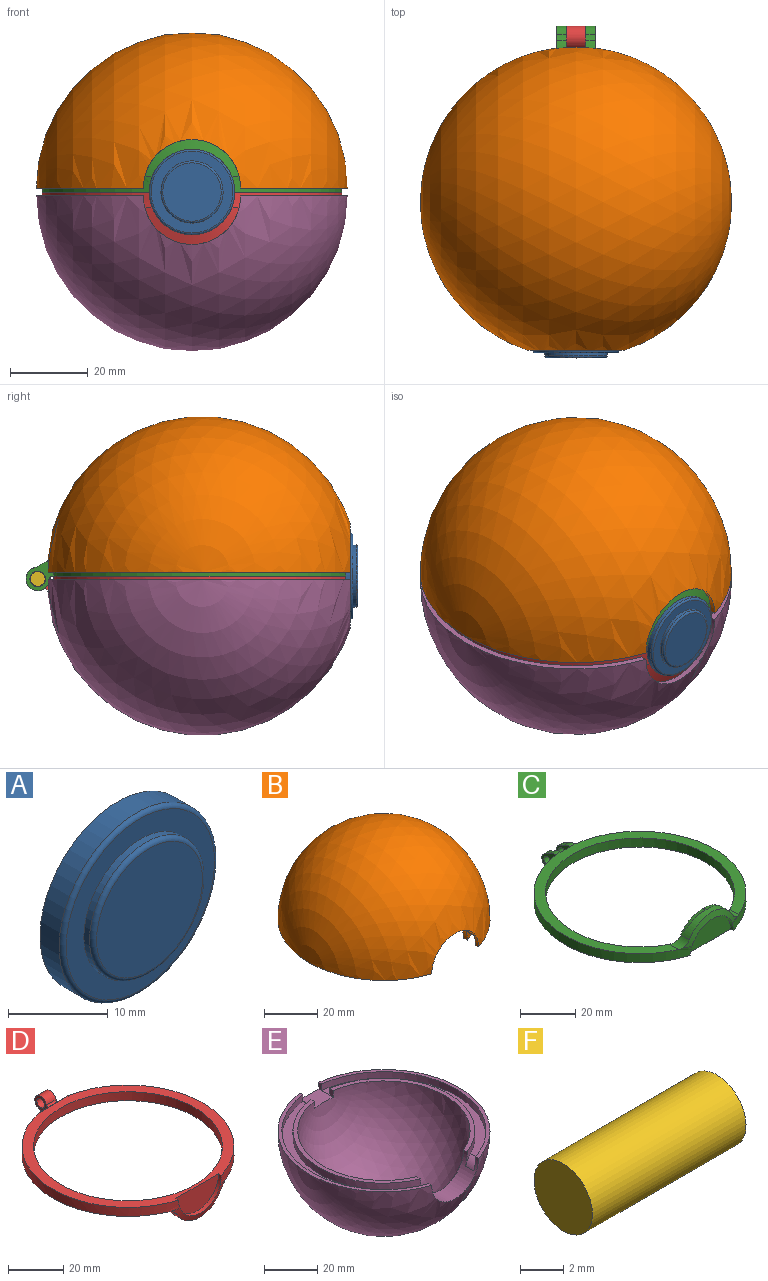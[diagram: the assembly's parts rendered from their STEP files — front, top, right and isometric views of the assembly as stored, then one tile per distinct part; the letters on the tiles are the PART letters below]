
ASSEMBLY  parts=6 mates=5
PART A: 7 faces, bbox 23.8x4.5x23.8 mm
  f0: cylinder r=11mm len=22mm, axis (0,1,0), area 186.6mm2, adj f2,f6
  f1: plane 21x21mm, normal (0,-1,0), area 145.3mm2, adj f3,f6
  f2: plane 22x22mm, normal (0,1,0), area 380.1mm2, adj f0
  f3: cylinder r=8mm len=16mm, axis (0,1,0), area 40.2mm2, adj f1,f5
  f4: plane 15x15mm, normal (0,-1,0), area 176.7mm2, adj f5
  f5: torus R=7.5mm, axis (0,-1,0), area 38.6mm2, adj f3,f4
  f6: torus R=10.5mm, axis (0,-1,0), area 53.4mm2, adj f0,f1
PART B: 18 faces, bbox 80x80x40 mm
  f0: plane 65.88x29.3mm, normal (0,0,-1), area 156.8mm2, adj f1,f8,f12,f17
  f1: sphere r=32.5mm, area 6350.2mm2, adj f0,f7,f12,f15,f16,f17
  f2: cylinder r=34.3mm len=66.38mm, axis (0,0,-1), area 272.3mm2, adj f4,f7,f12,f14,f16
  f3: cylinder r=38.5mm len=75.03mm, axis (0,0,-1), area 312mm2, adj f4,f11,f12,f14,f16
  f4: plane 73.39x33.5mm, normal (0,0,-1), area 391.7mm2, adj f2,f3,f14,f16
  f5: sphere r=40mm, area 9770.1mm2, adj f6,f11,f12,f15,f16,f17
  f6: plane 77.68x35mm, normal (0,0,-1), area 158.4mm2, adj f5,f9,f12,f17
  f7: plane 65.88x29.3mm, normal (0,0,-1), area 156.8mm2, adj f1,f2,f12,f16
  f8: cylinder r=34.3mm len=66.38mm, axis (0,0,-1), area 272.3mm2, adj f0,f10,f12,f13,f17
  f9: cylinder r=38.5mm len=75.03mm, axis (0,0,-1), area 312mm2, adj f6,f10,f12,f13,f17
  f10: plane 73.39x33.5mm, normal (0,0,-1), area 391.7mm2, adj f8,f9,f13,f17
  f11: plane 77.68x35mm, normal (0,0,-1), area 158.4mm2, adj f3,f5,f12,f16
  f12: cylinder r=12.5mm len=25mm, axis (0,1,0), area 261.2mm2, adj f0,f1,f2,f3,f5,f6,f7,f8
  f13: cylinder r=5mm len=6.29mm, axis (0,1,0), area 24.7mm2, adj f8,f9,f10,f12
  f14: cylinder r=5mm len=6.29mm, axis (0,1,0), area 24.7mm2, adj f2,f3,f4,f12
  f15: plane 10.05x7.97mm, normal (0,0,-1), area 75.5mm2, adj f1,f5,f16,f17
  f16: plane 7.72x3.1mm, normal (-1,0,0), area 10.8mm2, adj f1,f2,f3,f4,f5,f7,f11,f15
  f17: plane 7.72x3.1mm, normal (1,0,0), area 10.8mm2, adj f0,f1,f5,f6,f8,f9,f10,f15
PART C: 30 faces, bbox 77x85.6x18.1 mm
  f0: cylinder r=5mm len=2.5mm, axis (1,0,0), area 4.7mm2, adj f2,f20,f22,f28
  f1: cylinder r=1mm len=2.5mm, axis (-1,0,0), area 3.8mm2, adj f3,f5,f21,f27
  f2: cylinder r=5mm len=3.04mm, axis (1,0,0), area 8.2mm2, adj f0,f10,f20,f28
  f3: cylinder r=3mm len=5.99mm, axis (-1,0,0), area 32.8mm2, adj f1,f21,f24,f27
  f4: cylinder r=2mm len=4mm, axis (-1,0,0), area 31.4mm2, adj f21,f27
  f5: plane 77x75.26mm, normal (0,0,-1), area 905mm2, adj f1,f6,f8,f9,f18,f19,f20,f21
  f6: cylinder r=38.5mm len=75.29mm, axis (0,0,-1), area 421.3mm2, adj f5,f10,f12,f16,f19,f21
  f7: plane 1.93x0.79mm, normal (0,0.26,0.96), area 1.3mm2, adj f11,f13,f14,f15
  f8: cylinder r=34.3mm len=68.6mm, axis (0,0,-1), area 863.2mm2, adj f5,f10,f11,f16,f17
  f9: cylinder r=38.5mm len=75.29mm, axis (0,0,-1), area 421.3mm2, adj f5,f10,f12,f17,f19,f20
  f10: plane 77x73.68mm, normal (0,0,1), area 824.7mm2, adj f2,f6,f8,f9,f16,f17,f20,f21
  f11: bspline ~27.63x8.98mm, area 174.8mm2, adj f7,f8,f13,f14,f15,f16,f17
  f12: bspline ~27.97x10.28mm, area 75.1mm2, adj f6,f9,f15,f16,f17,f19
  f13: bspline ~14.62x12.35mm, area 19.7mm2, adj f7,f11,f15
  f14: bspline ~14.67x12.38mm, area 19.6mm2, adj f7,f11,f15
  f15: cylinder r=12.5mm len=22.24mm, axis (0,1,0), area 84.3mm2, adj f7,f11,f12,f13,f14,f16,f17
  f16: cylinder r=5mm len=5.97mm, axis (0,1,0), area 24.8mm2, adj f6,f8,f10,f11,f12,f15
  f17: cylinder r=5mm len=5.97mm, axis (0,1,0), area 24.8mm2, adj f8,f9,f10,f11,f12,f15
  f18: plane 22x11mm, normal (0,-1,0), area 190.1mm2, adj f5,f19
  f19: cylinder r=11mm len=22mm, axis (0,-1,0), area 54.8mm2, adj f5,f6,f9,f12,f18
  f20: plane 7.75x7.18mm, normal (1,0,0), area 25.8mm2, adj f0,f2,f5,f9,f10,f22,f23,f25
  f21: plane 7.75x7.18mm, normal (-1,0,0), area 25.8mm2, adj f1,f3,f4,f5,f6,f10,f24,f26
  f22: cylinder r=3mm len=5.99mm, axis (-1,0,0), area 32.8mm2, adj f0,f20,f25,f28
  f23: cylinder r=2mm len=4mm, axis (-1,0,0), area 31.4mm2, adj f20,f28
  f24: cylinder r=5mm len=2.5mm, axis (1,0,0), area 4.7mm2, adj f3,f21,f26,f27
  f25: cylinder r=1mm len=2.5mm, axis (-1,0,0), area 3.8mm2, adj f5,f20,f22,f28
  f26: cylinder r=5mm len=3.04mm, axis (1,0,0), area 8.2mm2, adj f10,f21,f24,f27
  f27: plane 7.75x7.18mm, normal (1,0,0), area 25.8mm2, adj f1,f3,f4,f5,f10,f24,f26,f29
  f28: plane 7.75x7.18mm, normal (-1,0,0), area 25.8mm2, adj f0,f2,f5,f10,f22,f23,f25,f29
  f29: plane 5x4mm, normal (0,1,0), area 20mm2, adj f5,f10,f27,f28
PART D: 25 faces, bbox 77x85.9x16.7 mm
  f0: cylinder r=2mm len=5mm, axis (-1,0,0), area 62.8mm2, adj f22,f24
  f1: cylinder r=3mm len=6mm, axis (-1,0,0), area 77.9mm2, adj f3,f20,f22,f24
  f2: cylinder r=0.5mm len=5mm, axis (1,0,0), area 3.9mm2, adj f3,f19,f22,f24
  f3: cylinder r=1mm len=5mm, axis (1,0,0), area 5.7mm2, adj f1,f2,f22,f24
  f4: plane 77x74.57mm, normal (0,0,1), area 897.5mm2, adj f5,f8,f9,f15,f16,f19
  f5: cylinder r=38.5mm len=75.29mm, axis (0,0,1), area 420.5mm2, adj f4,f7,f11,f15,f18,f19,f23
  f6: plane 1.93x0.79mm, normal (0,0.26,-0.96), area 1.3mm2, adj f10,f12,f13,f14
  f7: plane 77x73.59mm, normal (0,0,-1), area 824.3mm2, adj f5,f8,f9,f17,f18,f20,f21,f22
  f8: cylinder r=34.3mm len=68.6mm, axis (0,0,1), area 863.2mm2, adj f4,f7,f10,f17,f18
  f9: cylinder r=38.5mm len=75.29mm, axis (0,0,1), area 420.5mm2, adj f4,f7,f11,f15,f17,f19,f21
  f10: bspline ~27.63x8.98mm, area 174.8mm2, adj f6,f8,f12,f13,f14,f17,f18
  f11: bspline ~27.97x10.28mm, area 75.1mm2, adj f5,f9,f14,f15,f17,f18
  f12: bspline ~15.41x12.39mm, area 19.7mm2, adj f6,f10,f14
  f13: bspline ~15.49x12.39mm, area 19.7mm2, adj f6,f10,f14
  f14: cylinder r=12.5mm len=22.24mm, axis (0,1,0), area 84.3mm2, adj f6,f10,f11,f12,f13,f17,f18
  f15: cylinder r=11mm len=22mm, axis (0,-1,0), area 54.8mm2, adj f4,f5,f9,f11,f16
  f16: plane 22x11mm, normal (0,-1,0), area 190.1mm2, adj f4,f15
  f17: cylinder r=5mm len=5.97mm, axis (0,1,0), area 24.8mm2, adj f7,f8,f9,f10,f11,f14
  f18: cylinder r=5mm len=5.97mm, axis (0,1,0), area 24.8mm2, adj f5,f7,f8,f10,f11,f14
  f19: cylinder r=0.5mm len=15.87mm, axis (-1,0,0), area 10.2mm2, adj f2,f4,f5,f9,f21,f23
  f20: cylinder r=3mm len=5mm, axis (-1,0,0), area 11.8mm2, adj f1,f7,f22,f24
  f21: plane 3.5x2.5mm, normal (0,1,0), area 8.7mm2, adj f7,f9,f19,f22
  f22: plane 7.18x6.25mm, normal (1,0,0), area 20.7mm2, adj f0,f1,f2,f3,f7,f20,f21
  f23: plane 3.5x2.5mm, normal (0,1,0), area 8.7mm2, adj f5,f7,f19,f24
  f24: plane 7.18x6.25mm, normal (-1,0,0), area 20.7mm2, adj f0,f1,f2,f3,f7,f20,f23
PART E: 18 faces, bbox 80x80x40 mm
  f0: plane 65.88x29.3mm, normal (0,0,1), area 156.8mm2, adj f1,f8,f12,f17
  f1: sphere r=32.5mm, area 6350.2mm2, adj f0,f7,f12,f15,f16,f17
  f2: cylinder r=34.3mm len=66.38mm, axis (0,0,1), area 272.3mm2, adj f4,f7,f12,f14,f16
  f3: cylinder r=38.5mm len=75.03mm, axis (0,0,1), area 312mm2, adj f4,f11,f12,f14,f16
  f4: plane 73.39x33.5mm, normal (0,0,1), area 391.7mm2, adj f2,f3,f14,f16
  f5: sphere r=40mm, area 9770.1mm2, adj f6,f11,f12,f15,f16,f17
  f6: plane 77.68x35mm, normal (0,0,1), area 158.4mm2, adj f5,f9,f12,f17
  f7: plane 65.88x29.3mm, normal (0,0,1), area 156.8mm2, adj f1,f2,f12,f16
  f8: cylinder r=34.3mm len=66.38mm, axis (0,0,1), area 272.3mm2, adj f0,f10,f12,f13,f17
  f9: cylinder r=38.5mm len=75.03mm, axis (0,0,1), area 312mm2, adj f6,f10,f12,f13,f17
  f10: plane 73.39x33.5mm, normal (0,0,1), area 391.7mm2, adj f8,f9,f13,f17
  f11: plane 77.68x35mm, normal (0,0,1), area 158.4mm2, adj f3,f5,f12,f16
  f12: cylinder r=12.5mm len=25mm, axis (0,1,0), area 261.2mm2, adj f0,f1,f2,f3,f5,f6,f7,f8
  f13: cylinder r=5mm len=6.29mm, axis (0,1,0), area 24.7mm2, adj f8,f9,f10,f12
  f14: cylinder r=5mm len=6.29mm, axis (0,1,0), area 24.7mm2, adj f2,f3,f4,f12
  f15: plane 10.05x7.97mm, normal (0,0,1), area 75.5mm2, adj f1,f5,f16,f17
  f16: plane 7.72x3.1mm, normal (-1,0,0), area 10.8mm2, adj f1,f2,f3,f4,f5,f7,f11,f15
  f17: plane 7.72x3.1mm, normal (1,0,0), area 10.8mm2, adj f0,f1,f5,f6,f8,f9,f10,f15
PART F: 3 faces, bbox 10x3.8x3.8 mm
  f0: plane 3.8x3.8mm, normal (-1,0,0), area 11.3mm2, adj f1
  f1: cylinder r=1.9mm len=10mm, axis (1,0,0), area 119.4mm2, adj f0,f2
  f2: plane 3.8x3.8mm, normal (1,0,0), area 11.3mm2, adj f1
PLACE A t=(64.68,17.84,38.14)mm
PLACE B t=(64.68,-1.91,-10.86)mm
PLACE C t=(64.68,-1.91,38.14)mm
PLACE D t=(64.68,-1.91,88.14)mm
PLACE E t=(64.68,-1.91,137.14)mm
PLACE F t=(34.68,-1.91,38.14)mm
MATE fastened A.f0 <-> C.f19  axis (0,1,0) through (64.68,-37.41,-11.86)mm
MATE fastened F.f1 <-> C.f3  axis (1,0,0) through (69.68,40.44,-12.61)mm
MATE fastened C.f6 <-> B.f3  axis (0,0,1) through (64.68,-1.91,-7.86)mm
MATE fastened D.f8 <-> C.f8  axis (0,0,1) through (64.68,-1.91,-11.86)mm
MATE fastened E.f3 <-> D.f5  axis (0,0,1) through (64.68,-1.91,-15.86)mm
